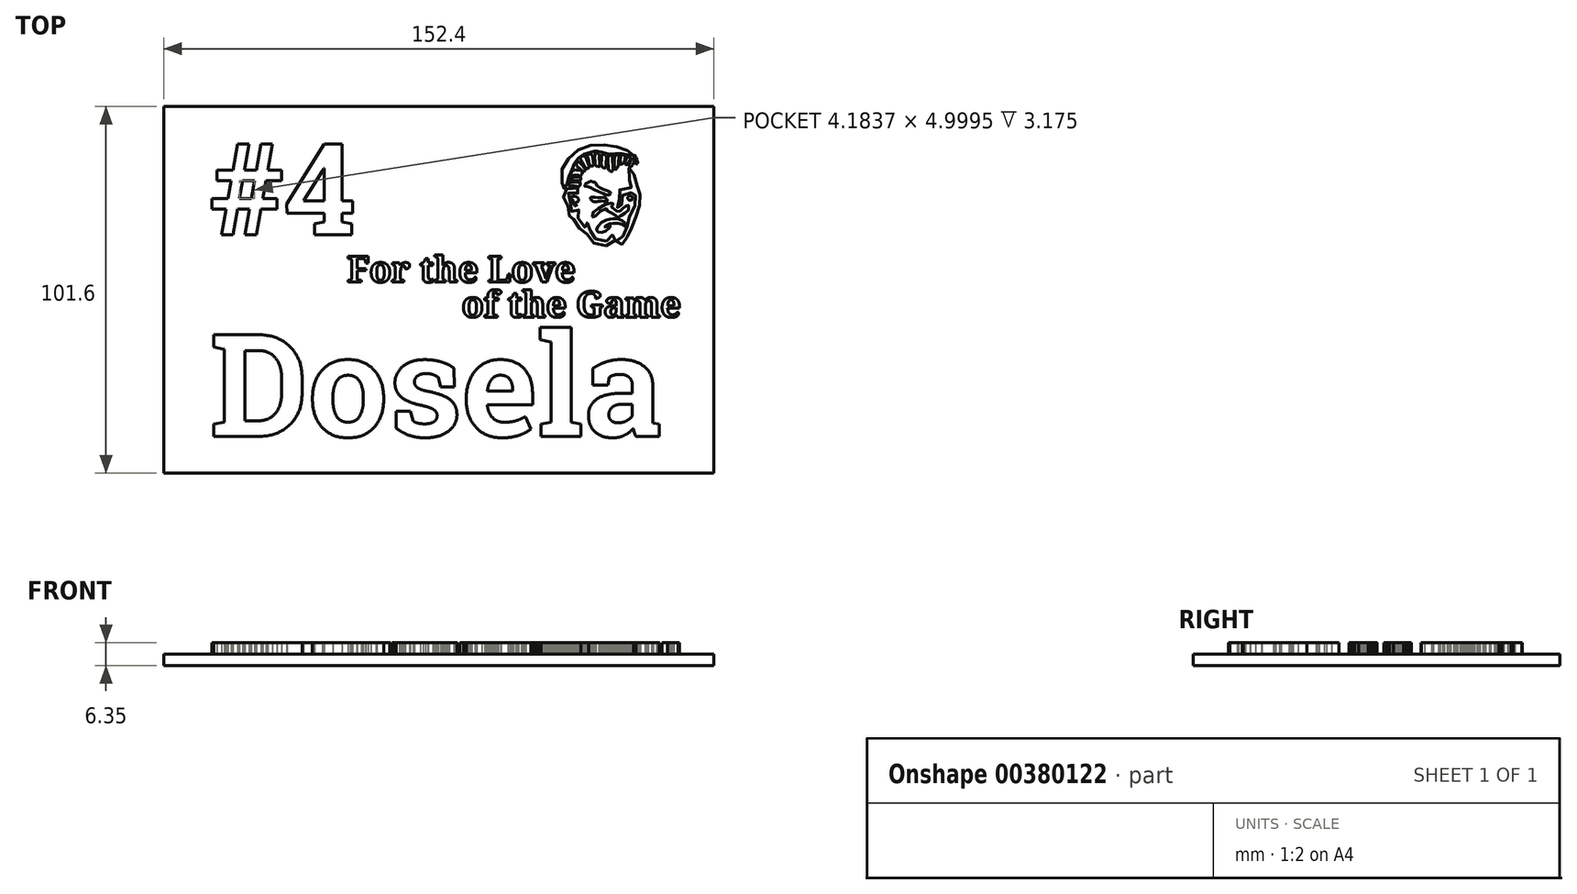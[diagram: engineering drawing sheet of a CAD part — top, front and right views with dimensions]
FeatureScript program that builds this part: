
annotation { "Feature Type Name" : "Feature", "Feature Type Description" : "" }
export const myFeature = defineFeature(function(context is Context, id is Id, definition is map)
    precondition{}
    {
        {
            var Q0;
            Q0=qCreatedBy(makeId("Top.planeOp"),FACE);
            var sketch = newSketch(context, id + "F0", { "sketchPlane" : qUnion([Q0])});
            skLineSegment(sketch, "E0.bottom", {"start": v(-75.13, 26) * mm, "end": v(77.27, 26) * mm});
            skLineSegment(sketch, "E0.top", {"start": v(-75.13, -75.6) * mm, "end": v(77.27, -75.6) * mm});
            skLineSegment(sketch, "E0.left", {"start": v(-75.13, 26) * mm, "end": v(-75.13, -75.6) * mm});
            skLineSegment(sketch, "E0.right", {"start": v(77.27, 26) * mm, "end": v(77.27, -75.6) * mm});
            skSolve(sketch);
        }
        {
            var Q0;
            Q0=makeQuery(id+"F0.imprint","IMPRINT",FACE,{"disambiguationData":[TD([[makeQuery(id+"F0.imprint","IMPRINT",EDGE,{"derivedFrom":sQuery(id+"F0.wireOp",EDGE,"E0.bottom")}),-1.0]])]});
            var sketch = newSketch(context, id + "F1", { "sketchPlane" : qUnion([Q0])});
            skFitSpline(sketch, "E1", {"points": [v(47.57, -11.3) * mm, v(48.35, -11.04) * mm, v(48.7, -10.35) * mm, v(49.04, -9.7) * mm, v(49.57, -9.46) * mm, v(50.02, -9.78) * mm, v(50.06, -10.58) * mm, v(49.74, -11.5) * mm, v(49.1, -12.15) * mm, v(47.63, -12.55) * mm, v(46.12, -12.5) * mm, v(44.61, -12.12) * mm, v(43.38, -11.34) * mm, v(42.6, -10.32) * mm, v(42.24, -9.52) * mm, v(42.15, -9.31) * mm, v(41.34, -8.82) * mm, v(40.33, -8.02) * mm, v(39.44, -7.2) * mm, v(38.67, -6.1) * mm, v(38.42, -5) * mm, v(38.42, -4.22) * mm, v(38.35, -4.2) * mm, v(37.68, -4.39) * mm, v(37.16, -4.27) * mm, v(36.95, -3.72) * mm, v(36.86, -2.5) * mm, v(36.8, -1.48) * mm, v(36.67, -1.07) * mm, v(35.77, 0.2) * mm, v(35.58, 1.07) * mm, v(35.86, 2.13) * mm, v(36.18, 2.7) * mm, v(36.53, 3.12) * mm, v(37.23, 3.22) * mm, v(39.03, 3.4) * mm, v(39.82, 3.34) * mm, v(40.19, 3.09) * mm, v(40.23, 2.45) * mm, v(39.66, 1.98) * mm, v(38.93, 1.9) * mm, v(38.59, 2.03) * mm, v(37.24, 2.03) * mm, v(36.72, 1.65) * mm, v(36.72, 0.85) * mm, v(37.32, -0.2) * mm, v(37.77, -1.18) * mm, v(37.85, -2.09) * mm, v(37.9, -3.1) * mm, v(37.99, -3.1) * mm, v(38.63, -3.1) * mm, v(39.4, -2.76) * mm, v(39.72, -2.59) * mm, v(39.8, -2.7) * mm, v(39.73, -3.22) * mm, v(39.6, -4) * mm, v(39.6, -4.77) * mm, v(40.1, -5.82) * mm, v(41.16, -7.15) * mm, v(41.6, -7.53) * mm, v(41.9, -7.56) * mm, v(41.89, -7.44) * mm, v(41.82, -6.61) * mm, v(42, -6.23) * mm, v(42.5, -6.3) * mm, v(42.8, -6.61) * mm, v(43.05, -7.98) * mm, v(43.22, -8.82) * mm, v(43.51, -9.54) * mm, v(44.12, -10.4) * mm, v(45.11, -11.01) * mm, v(46.32, -11.33) * mm, v(47.57, -11.3) * mm]});
            skFitSpline(sketch, "E2", {"points": [v(47.8, -7.3) * mm, v(47.13, -7.42) * mm, v(47.01, -7.42) * mm, v(47.13, -7.18) * mm, v(48.11, -6.65) * mm, v(49.11, -6.46) * mm, v(50.54, -6.45) * mm, v(51.76, -6.67) * mm, v(52.61, -7.21) * mm, v(52.82, -7.33) * mm, v(52.97, -7.12) * mm, v(52.7, -6.5) * mm, v(52.11, -5.74) * mm, v(50.6, -5.18) * mm, v(49.08, -5.16) * mm, v(48.46, -5.24) * mm, v(47.16, -5.6) * mm, v(45.65, -6.61) * mm, v(44.86, -7.78) * mm, v(44.9, -8.5) * mm, v(45.47, -8.94) * mm, v(46.7, -8.8) * mm, v(47.75, -8.16) * mm, v(48.56, -7.4) * mm, v(48.6, -7.12) * mm, v(47.8, -7.3) * mm]});
            skFitSpline(sketch, "E3", {"points": [v(51.85, -12.22) * mm, v(51.05, -12.44) * mm, v(50.33, -12.28) * mm, v(50.13, -11.73) * mm, v(50.52, -11.04) * mm, v(51.15, -10.86) * mm, v(51.76, -10.57) * mm, v(52.13, -10) * mm, v(52.3, -9.2) * mm, v(52.67, -8.25) * mm, v(53.2, -7.5) * mm, v(53.55, -6.76) * mm, v(53.63, -5.82) * mm, v(53.78, -4.85) * mm, v(54.49, -3.73) * mm, v(55.3, -2.73) * mm, v(55.42, -1.6) * mm, v(55.17, -0.4) * mm, v(55.2, 0.11) * mm, v(55.52, 1.32) * mm, v(55.57, 2.16) * mm, v(55.47, 2.42) * mm, v(54.99, 2.38) * mm, v(54.56, 2.14) * mm, v(53.7, 2.1) * mm, v(52.55, 2.06) * mm, v(52.07, 1.77) * mm, v(51.98, 1.02) * mm, v(52.2, 0.28) * mm, v(52.08, -0.6) * mm, v(51.72, -1.24) * mm, v(51.47, -1.75) * mm, v(51.5, -2.22) * mm, v(51.32, -2.4) * mm, v(50.6, -2.13) * mm, v(50.38, -1.6) * mm, v(50.64, -0.97) * mm, v(51, -0.17) * mm, v(51.06, 0.44) * mm, v(50.78, 1.07) * mm, v(50.66, 1.97) * mm, v(51.18, 2.9) * mm, v(52.12, 3.24) * mm, v(53.3, 3.36) * mm, v(54.52, 3.48) * mm, v(54.66, 3.6) * mm, v(54.38, 3.97) * mm, v(54, 4.8) * mm, v(53.79, 6.28) * mm, v(53.9, 7.94) * mm, v(53.79, 8.9) * mm, v(53.79, 9.1) * mm, v(54.03, 9.04) * mm, v(54.76, 8.52) * mm, v(55.13, 7.38) * mm, v(55.34, 5.97) * mm, v(55.56, 4.72) * mm, v(56.14, 3.87) * mm, v(56.71, 3.56) * mm, v(57.08, 2.91) * mm, v(56.95, 1.93) * mm, v(56.51, 0.55) * mm, v(56.4, -0.31) * mm, v(56.62, -1.36) * mm, v(56.69, -2.19) * mm, v(56.32, -3.56) * mm, v(55.4, -4.86) * mm, v(54.62, -5.8) * mm, v(54.5, -7.08) * mm, v(54.37, -8.24) * mm, v(53.76, -9.26) * mm, v(53.43, -9.82) * mm, v(53.28, -10.59) * mm, v(53.14, -11.27) * mm, v(52.34, -11.95) * mm, v(51.85, -12.22) * mm]});
            skFitSpline(sketch, "E4", {"points": [v(51.65, -4.28) * mm, v(52.13, -3.81) * mm, v(53.02, -3.37) * mm, v(53.66, -2.72) * mm, v(53.77, -1.9) * mm, v(53.38, -1.13) * mm, v(53.21, -1.15) * mm, v(53, -1.68) * mm, v(52.43, -2.14) * mm, v(51.8, -2.46) * mm, v(51.42, -2.92) * mm, v(50.93, -3.27) * mm, v(50.6, -3.17) * mm, v(50.13, -2.68) * mm, v(49.7, -2.46) * mm, v(49.28, -2.45) * mm, v(49, -1.98) * mm, v(49.06, -1.41) * mm, v(49.39, -0.94) * mm, v(49.4, -0.71) * mm, v(48.82, -0.74) * mm, v(47.56, -0.99) * mm, v(45.6, -2.02) * mm, v(44.06, -3.24) * mm, v(43.57, -3.77) * mm, v(43.7, -4.86) * mm, v(43.9, -4.88) * mm, v(44.45, -4.27) * mm, v(46.1, -2.93) * mm, v(47.41, -2.3) * mm, v(47.63, -2.3) * mm, v(47.73, -2.85) * mm, v(48.15, -3.33) * mm, v(48.9, -3.44) * mm, v(49.24, -3.55) * mm, v(49.84, -4.18) * mm, v(50.54, -4.68) * mm, v(51.18, -4.66) * mm, v(51.65, -4.28) * mm]});
            skFitSpline(sketch, "E5", {"points": [v(54.73, 0.39) * mm, v(54.77, 0.82) * mm, v(54.18, 1.2) * mm, v(53.55, 1.02) * mm, v(53.47, 0.3) * mm, v(54.02, 0) * mm, v(54.73, 0.39) * mm]});
            skFitSpline(sketch, "E6", {"points": [v(44.44, -0.47) * mm, v(43.66, -0.25) * mm, v(43.08, 0.44) * mm, v(43.14, 0.75) * mm, v(43.78, 0.8) * mm, v(46.74, 0.78) * mm, v(47.17, 0.7) * mm, v(47.78, -0.13) * mm, v(47.64, -0.32) * mm, v(46.64, -0.26) * mm, v(45.29, -0.32) * mm, v(44.44, -0.47) * mm]});
            skFitSpline(sketch, "E7", {"points": [v(46.65, 1.86) * mm, v(47.46, 1.48) * mm, v(48.33, 1.53) * mm, v(48.69, 2.02) * mm, v(48.54, 2.32) * mm, v(47.26, 2.83) * mm, v(45.32, 3.72) * mm, v(44.79, 4.23) * mm, v(44.53, 4.83) * mm, v(44.13, 5) * mm, v(43.88, 5) * mm, v(43.34, 5.26) * mm, v(43.09, 5.3) * mm, v(42.9, 5.05) * mm, v(42.6, 5.07) * mm, v(42.3, 4.85) * mm, v(42.2, 4.73) * mm, v(41.9, 4.72) * mm, v(41.8, 4.5) * mm, v(41.38, 4.05) * mm, v(41.56, 3.84) * mm, v(42.59, 3.74) * mm, v(43.78, 3.19) * mm, v(46.65, 1.86) * mm]});
            skFitSpline(sketch, "E8", {"points": [v(39.09, -1.2) * mm, v(38.85, -1.02) * mm, v(39.04, -0.63) * mm, v(39.6, -0.4) * mm, v(39.72, 0.33) * mm, v(39.01, 1.06) * mm, v(38.23, 1.1) * mm, v(37.7, 0.65) * mm, v(37.83, 0.29) * mm, v(38.12, 0.15) * mm, v(38.31, -0.34) * mm, v(38.52, -1.23) * mm, v(38.92, -1.63) * mm, v(39.18, -1.51) * mm, v(39.26, -1.2) * mm, v(39.09, -1.2) * mm]});
            skFitSpline(sketch, "E9", {"points": [v(35.18, 4.73) * mm, v(35.4, 3.4) * mm, v(35.76, 3.05) * mm, v(35.87, 3.13) * mm, v(36.08, 3.42) * mm, v(36.43, 3.67) * mm, v(36.66, 4.42) * mm, v(36.6, 5.36) * mm, v(37.02, 6.1) * mm, v(37.15, 6.7) * mm, v(37.23, 7.46) * mm, v(37.88, 8.4) * mm, v(38.45, 9.02) * mm, v(38.56, 9.75) * mm, v(38.74, 10.4) * mm, v(39.17, 10.98) * mm, v(39.64, 11.29) * mm, v(39.78, 11.9) * mm, v(40.12, 12.28) * mm, v(40.85, 12.68) * mm, v(41.65, 12.77) * mm, v(42.03, 12.99) * mm, v(42.91, 13.25) * mm, v(43.49, 13.17) * mm, v(43.91, 13.25) * mm, v(44.22, 13.54) * mm, v(44.87, 13.6) * mm, v(45.62, 13.32) * mm, v(46.3, 13.31) * mm, v(46.91, 13.3) * mm, v(47.51, 12.81) * mm, v(48.11, 12.71) * mm, v(48.8, 12.83) * mm, v(49.39, 12.68) * mm, v(50.13, 12.89) * mm, v(50.83, 12.96) * mm, v(51.35, 12.83) * mm, v(51.87, 12.94) * mm, v(52.53, 12.95) * mm, v(53.18, 12.6) * mm, v(53.93, 12.6) * mm, v(54.48, 12.4) * mm, v(54.65, 12.18) * mm, v(55.03, 12.55) * mm, v(54.73, 12.89) * mm, v(53.9, 13.45) * mm, v(51.53, 14.51) * mm, v(50.44, 14.76) * mm, v(49.1, 15.08) * mm, v(45.83, 15.4) * mm, v(43.17, 15.22) * mm, v(40.97, 14.54) * mm, v(38.6, 13.18) * mm, v(36.98, 11.4) * mm, v(35.34, 9.1) * mm, v(35.2, 8.1) * mm, v(35.18, 4.73) * mm]});
            skFitSpline(sketch, "E10", {"points": [v(39.4, 5) * mm, v(39.96, 4.99) * mm, v(40.23, 4.82) * mm, v(40.1, 4) * mm, v(39.64, 3.78) * mm, v(38.94, 3.9) * mm, v(37.89, 3.94) * mm, v(37.45, 3.8) * mm, v(37.1, 4.04) * mm, v(37.54, 4.84) * mm, v(38.3, 5) * mm, v(39.4, 5) * mm]});
            skFitSpline(sketch, "E11", {"points": [v(37.48, 5.07) * mm, v(37.11, 4.96) * mm, v(36.94, 5.2) * mm, v(37.34, 5.9) * mm, v(37.75, 6.14) * mm, v(39.96, 6.47) * mm, v(40.35, 6.2) * mm, v(40.47, 5.65) * mm, v(40.11, 5.36) * mm, v(39.64, 5.4) * mm, v(38.37, 5.41) * mm, v(37.48, 5.07) * mm]});
            skFitSpline(sketch, "E12", {"points": [v(38.14, 6.82) * mm, v(39.68, 6.88) * mm, v(40, 6.74) * mm, v(40.54, 7) * mm, v(40.85, 7.85) * mm, v(40.67, 8.1) * mm, v(39.1, 8.4) * mm, v(38.41, 8.3) * mm, v(37.9, 7.73) * mm, v(37.48, 6.86) * mm, v(37.68, 6.74) * mm, v(38.14, 6.82) * mm]});
            skFitSpline(sketch, "E13", {"points": [v(39.26, 9.59) * mm, v(41, 8.1) * mm, v(41.32, 7.94) * mm, v(41.68, 8.33) * mm, v(41.53, 8.74) * mm, v(40.44, 10.1) * mm, v(39.87, 10.6) * mm, v(39.5, 10.56) * mm, v(39.13, 10.09) * mm, v(39.26, 9.59) * mm]});
            skFitSpline(sketch, "E14", {"points": [v(40.75, 10.65) * mm, v(40.33, 11.47) * mm, v(40.46, 11.98) * mm, v(41.21, 12.34) * mm, v(41.77, 12.07) * mm, v(42.13, 11.12) * mm, v(42.72, 9.33) * mm, v(42.65, 8.96) * mm, v(42.12, 8.81) * mm, v(41.62, 9.07) * mm, v(40.75, 10.65) * mm]});
            skFitSpline(sketch, "E15", {"points": [v(42.43, 11.4) * mm, v(42.21, 12.24) * mm, v(42.3, 12.64) * mm, v(43, 12.81) * mm, v(43.54, 12.53) * mm, v(43.83, 11.13) * mm, v(44, 9.88) * mm, v(43.65, 9.47) * mm, v(42.94, 9.8) * mm, v(42.43, 11.4) * mm]});
            skFitSpline(sketch, "E16", {"points": [v(44.29, 12.06) * mm, v(44.36, 12.96) * mm, v(44.5, 13.26) * mm, v(44.93, 13.17) * mm, v(45.54, 12.55) * mm, v(45.55, 11.97) * mm, v(45.6, 9.45) * mm, v(45.5, 9.32) * mm, v(44.61, 9.6) * mm, v(44.4, 10.08) * mm, v(44.29, 12.06) * mm]});
            skFitSpline(sketch, "E17", {"points": [v(46.05, 10.51) * mm, v(46.15, 9.53) * mm, v(46.62, 9.04) * mm, v(47.1, 8.88) * mm, v(47.3, 9.08) * mm, v(47.48, 10.9) * mm, v(47.53, 12.07) * mm, v(47.34, 12.46) * mm, v(46.68, 12.84) * mm, v(46.32, 12.79) * mm, v(46.17, 11.97) * mm, v(46.05, 10.51) * mm]});
            skFitSpline(sketch, "E18", {"points": [v(48.03, 8.99) * mm, v(48.11, 8.48) * mm, v(48.48, 8.11) * mm, v(48.94, 7.92) * mm, v(49.21, 8.2) * mm, v(49.24, 10.23) * mm, v(49.16, 12.1) * mm, v(48.83, 12.47) * mm, v(48.44, 12.47) * mm, v(47.98, 12) * mm, v(47.93, 10.87) * mm, v(48.03, 8.99) * mm]});
            skFitSpline(sketch, "E19", {"points": [v(49.71, 9.45) * mm, v(49.86, 8.66) * mm, v(50.13, 8.48) * mm, v(50.3, 8.75) * mm, v(50.76, 9.43) * mm, v(50.85, 10.13) * mm, v(50.93, 12.16) * mm, v(50.81, 12.6) * mm, v(50.31, 12.66) * mm, v(49.83, 12.22) * mm, v(49.7, 11.19) * mm, v(49.71, 9.45) * mm]});
            skFitSpline(sketch, "E20", {"points": [v(51.32, 10.54) * mm, v(51.4, 11.84) * mm, v(51.7, 12.52) * mm, v(52.3, 12.55) * mm, v(52.72, 12.21) * mm, v(52.63, 11.54) * mm, v(52.29, 10.26) * mm, v(51.93, 10.06) * mm, v(51.44, 9.99) * mm, v(51.32, 10.54) * mm]});
            skFitSpline(sketch, "E21", {"points": [v(52.63, 10.38) * mm, v(52.83, 11.01) * mm, v(53.35, 11.9) * mm, v(53.66, 12.08) * mm, v(54.13, 11.71) * mm, v(53.9, 10.95) * mm, v(53.35, 10.1) * mm, v(53.17, 9.86) * mm, v(52.8, 9.99) * mm, v(52.63, 10.38) * mm]});
            skFitSpline(sketch, "E22", {"points": [v(53.86, 10.18) * mm, v(53.7, 9.9) * mm, v(53.81, 9.57) * mm, v(54.15, 9.28) * mm, v(54.42, 9.39) * mm, v(55.14, 10.6) * mm, v(55.26, 11.14) * mm, v(55.02, 11.54) * mm, v(54.8, 11.61) * mm, v(54.48, 11.27) * mm, v(53.86, 10.18) * mm]});
            skFitSpline(sketch, "E23", {"points": [v(55.24, 11.7) * mm, v(55.54, 11.38) * mm, v(55.58, 10.83) * mm, v(55.47, 10.49) * mm, v(55.7, 10.04) * mm, v(55.92, 10.02) * mm, v(56.2, 10.63) * mm, v(56.05, 10.85) * mm, v(55.85, 11.61) * mm, v(55.63, 12) * mm, v(55.42, 12.46) * mm, v(55.15, 12.4) * mm, v(55.09, 11.93) * mm, v(55.24, 11.7) * mm]});
            skText(sketch, "E24", { "text": "For the Love", "fontName": "NotoSerif-Bold.ttf"});
            skText(sketch, "E25", { "text": "of the Game", "fontName": "NotoSerif-Bold.ttf"});
            skText(sketch, "E26", { "text": "#4", "fontName": "RobotoSlab-Bold.ttf"});
            skText(sketch, "E27", { "text": "Dosela", "fontName": "RobotoSlab-Bold.ttf"});
            const initialGuessF1  = {"E24": [-0.02433, -0.0227, 1, 0, 0.00716], "E25": [0.00742, -0.0324, 1, 0, 0.00716], "E26": [-0.06243, -0.00956, 1, 0, 0.0254], "E27": [-0.06243, -0.06544, 1, 0, 0.0285]};
            skSetInitialGuess(sketch, initialGuessF1);
            skSolve(sketch);
        }
        {
            var Q0;
            Q0=qSketchRegion(id+"F0",true);
            extrude(context, id + "F2", {"entities" : qUnion([Q0]), "depth" : 3.17 * mm});
        }
        {
            var Q0;
            Q0=qSketchRegion(id+"F1",true);
            extrude(context, id + "F3", {"entities" : qUnion([Q0]), "operationType" : NewBodyOperationType.ADD, "depth" : 6.35 * mm});
        }
    });
